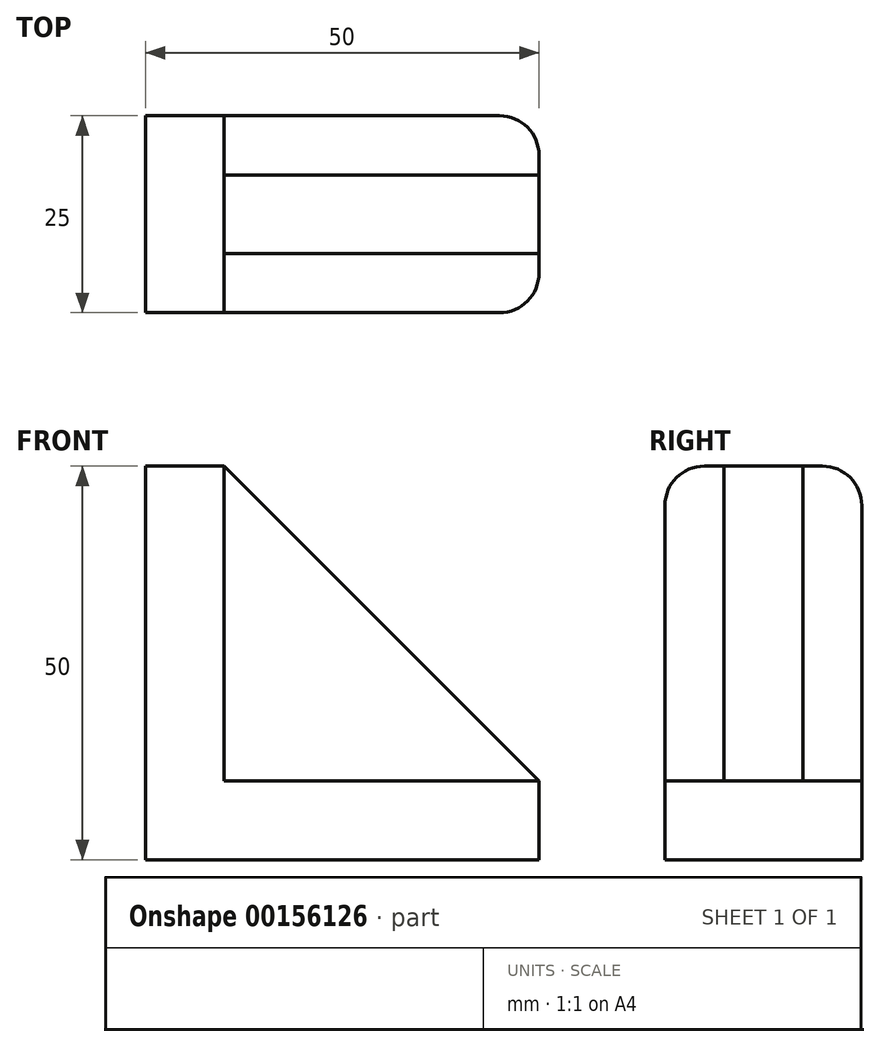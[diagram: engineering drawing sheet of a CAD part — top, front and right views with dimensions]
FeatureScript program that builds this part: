
annotation { "Feature Type Name" : "Feature", "Feature Type Description" : "" }
export const myFeature = defineFeature(function(context is Context, id is Id, definition is map)
    precondition{}
    {
        {
            var Q0;
            Q0=qCreatedBy(makeId("Front.planeOp"),FACE);
            var sketch = newSketch(context, id + "F0", { "sketchPlane" : qUnion([Q0])});
            skLineSegment(sketch, "E0.bottom", {"start": v(0, 0) * mm, "end": v(10, 0) * mm});
            skLineSegment(sketch, "E0.top", {"start": v(0, 50) * mm, "end": v(10, 50) * mm});
            skLineSegment(sketch, "E0.left", {"start": v(0, 0) * mm, "end": v(0, 50) * mm});
            skLineSegment(sketch, "E0.right", {"start": v(10, 0) * mm, "end": v(10, 50) * mm});
            skLineSegment(sketch, "E1.bottom", {"start": v(10, 0) * mm, "end": v(50, 0) * mm});
            skLineSegment(sketch, "E1.top", {"start": v(10, 10) * mm, "end": v(50, 10) * mm});
            skLineSegment(sketch, "E1.left", {"start": v(10, 0) * mm, "end": v(10, 10) * mm});
            skLineSegment(sketch, "E1.right", {"start": v(50, 0) * mm, "end": v(50, 10) * mm});
            skLineSegment(sketch, "E2", {"start": v(10, 50) * mm, "end": v(50, 10) * mm});
            skSolve(sketch);
        }
        {
            var Q0;
            Q0=makeQuery(id+"F0.imprint","IMPRINT",FACE,{"disambiguationData":[TD([[makeQuery(id+"F0.imprint","IMPRINT",EDGE,{"derivedFrom":sQuery(id+"F0.wireOp",EDGE,"E0.bottom")}),1.0]])]});
            var Q1;
            Q1=makeQuery(id+"F0.imprint","IMPRINT",FACE,{"disambiguationData":[TD([[makeQuery(id+"F0.imprint","IMPRINT",EDGE,{"derivedFrom":sQuery(id+"F0.wireOp",EDGE,"E1.bottom")}),1.0]])]});
            extrude(context, id + "F1", {"entities" : qUnion([Q0, Q1]), "endBound" : BoundingType.SYMMETRIC, "depth" : 25 * mm});
        }
        {
            var Q0;
            Q0=makeQuery(id+"F0.imprint","IMPRINT",FACE,{"disambiguationData":[TD([[makeQuery(id+"F0.imprint","IMPRINT",EDGE,{"derivedFrom":sQuery(id+"F0.wireOp",EDGE,"E0.right")}),-1.0]])]});
            extrude(context, id + "F2", {"entities" : qUnion([Q0]), "operationType" : NewBodyOperationType.ADD, "endBound" : BoundingType.SYMMETRIC, "depth" : 10 * mm});
        }
        {
            var Q0;
            Q0=makeQuery(id+"F1.opExtrude","CAP_EDGE",EDGE,{"disambiguationData":[OSD([sQuery(id+"F0.wireOp",EDGE,"E1.right")])],"isStart":false});
            var Q1;
            Q1=makeQuery(id+"F1.opExtrude","CAP_EDGE",EDGE,{"disambiguationData":[OSD([sQuery(id+"F0.wireOp",EDGE,"E1.right")])],"isStart":true});
            var Q2;
            Q2=makeQuery(id+"F1.opExtrude","CAP_EDGE",EDGE,{"disambiguationData":[OSD([sQuery(id+"F0.wireOp",EDGE,"E0.top")])],"isStart":true});
            var Q3;
            Q3=makeQuery(id+"F1.opExtrude","CAP_EDGE",EDGE,{"disambiguationData":[OSD([sQuery(id+"F0.wireOp",EDGE,"E0.top")])],"isStart":false});
            fillet(context, id + "F3", {"entities" : qUnion([Q0, Q1, Q2, Q3]), "radius" : 5 * mm, "tangentPropagation" : true, "allowEdgeOverflow" : false});
        }
    });
